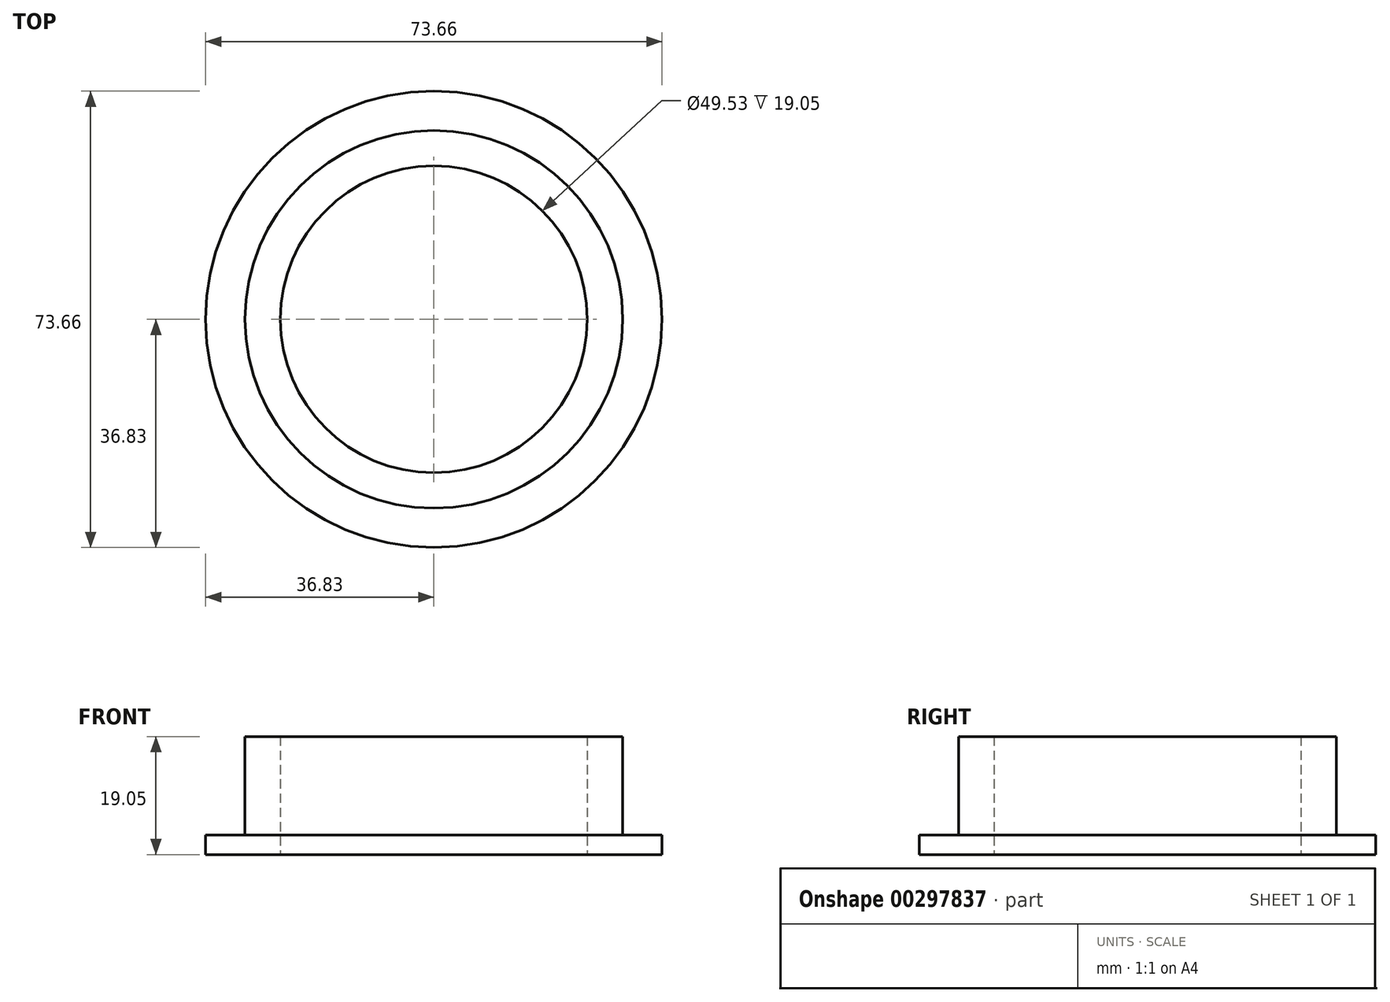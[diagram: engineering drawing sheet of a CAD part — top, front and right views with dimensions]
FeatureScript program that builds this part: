
annotation { "Feature Type Name" : "Feature", "Feature Type Description" : "" }
export const myFeature = defineFeature(function(context is Context, id is Id, definition is map)
    precondition{}
    {
        {
            var Q0;
            Q0=qCreatedBy(makeId("Top.planeOp"),FACE);
            var sketch = newSketch(context, id + "F0", { "sketchPlane" : qUnion([Q0])});
            skCircle(sketch, "E0", {"center": v(0, 0) * mm, "radius": 36.83 * mm});
            skCircle(sketch, "E1", {"center": v(0, 0) * mm, "radius": 24.77 * mm});
            skSolve(sketch);
        }
        {
            var Q0;
            Q0 = qSketchRegion(id + "F0", true);
            extrude(context, id + "F1", {"entities" : qUnion([Q0]), "depth" : 19.05 * mm});
        }
        {
            var Q0;
            Q0=qCreatedBy(makeId("Top.planeOp"),FACE);
            cPlane(context, id + "F2", {"entities" : qUnion([Q0]), "cplaneType" : CPlaneType.OFFSET, "offset" : 3.17 * mm, "width" : 152.4 * mm, "height" : 152.4 * mm});
        }
        {
            var Q0;
            Q0=qCreatedBy(id+"F2.planeOp",FACE);
            var sketch = newSketch(context, id + "F3", { "sketchPlane" : qUnion([Q0])});
            skCircle(sketch, "E2", {"center": v(0, 0) * mm, "radius": 30.48 * mm});
            skCircle(sketch, "E3", {"center": v(0, 0) * mm, "radius": 36.83 * mm});
            skSolve(sketch);
        }
        {
            var Q0;
            Q0 = qSketchRegion(id + "F3", true);
            var Q1;
            Q1=makeQuery(id+"F1.opExtrude","CAP_FACE",FACE,{"disambiguationData":[OSD([sQuery(id+"F0.wireOp",EDGE,"E0"),sQuery(id+"F0.wireOp",EDGE,"E1")])],"isStart":false});
            extrude(context, id + "F4", {"entities" : qUnion([Q0, Q1]), "operationType" : NewBodyOperationType.REMOVE, "depth" : 63.5 * mm});
        }
    });
